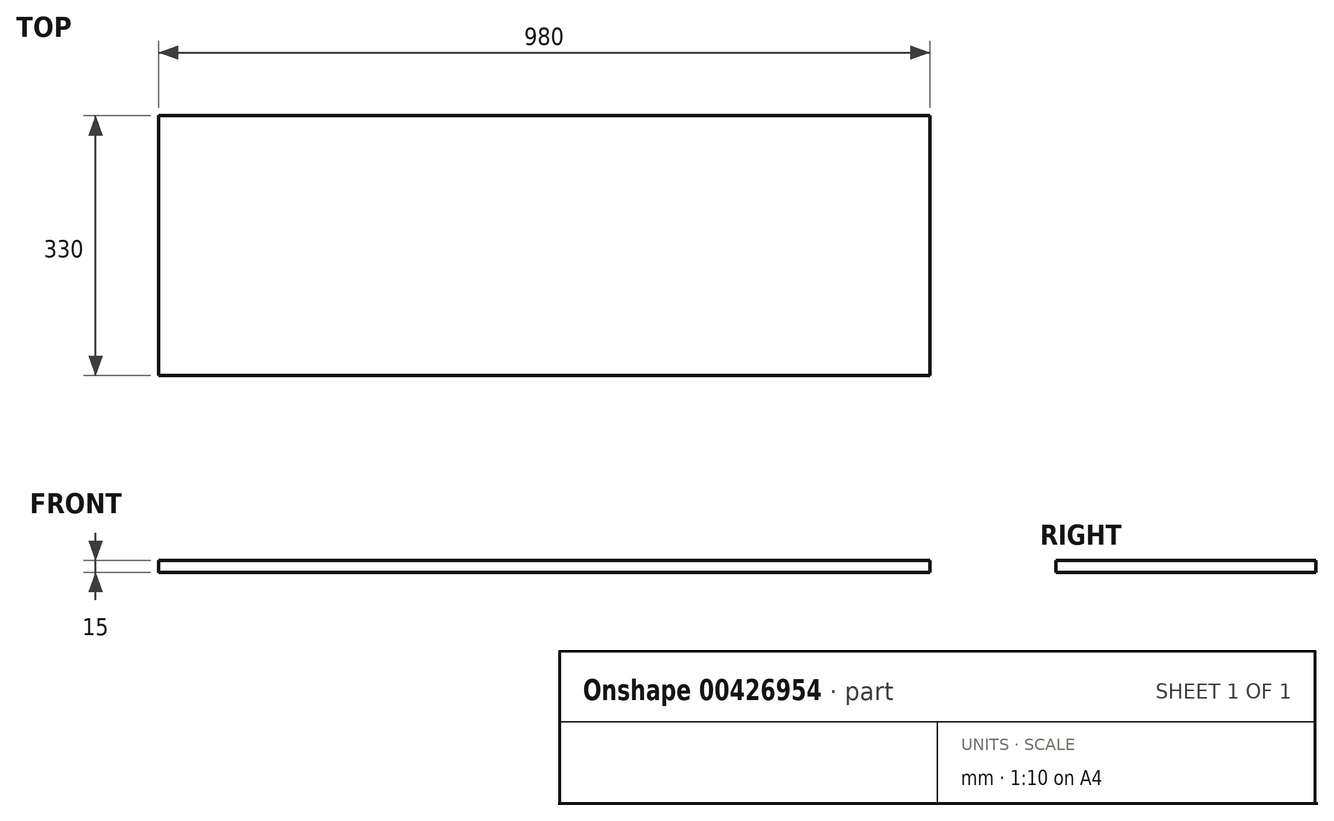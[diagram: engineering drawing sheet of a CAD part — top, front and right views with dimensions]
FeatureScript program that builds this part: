
annotation { "Feature Type Name" : "Feature", "Feature Type Description" : "" }
export const myFeature = defineFeature(function(context is Context, id is Id, definition is map)
    precondition{}
    {
        {
            var Q0;
            Q0=qCreatedBy(makeId("Top.planeOp"),FACE);
            var sketch = newSketch(context, id + "F0", { "sketchPlane" : qUnion([Q0])});
            skLineSegment(sketch, "E0.bottom", {"start": v(-518.94, -33.68) * mm, "end": v(461.06, -33.68) * mm});
            skLineSegment(sketch, "E0.top", {"start": v(-518.94, -363.68) * mm, "end": v(461.06, -363.68) * mm});
            skLineSegment(sketch, "E0.left", {"start": v(-518.94, -33.68) * mm, "end": v(-518.94, -363.68) * mm});
            skLineSegment(sketch, "E0.right", {"start": v(461.06, -33.68) * mm, "end": v(461.06, -363.68) * mm});
            skSolve(sketch);
        }
        {
            var Q0;
            Q0=qSketchRegion(id+"F0",true);
            extrude(context, id + "F1", {"entities" : qUnion([Q0]), "depth" : 15 * mm});
        }
    });
